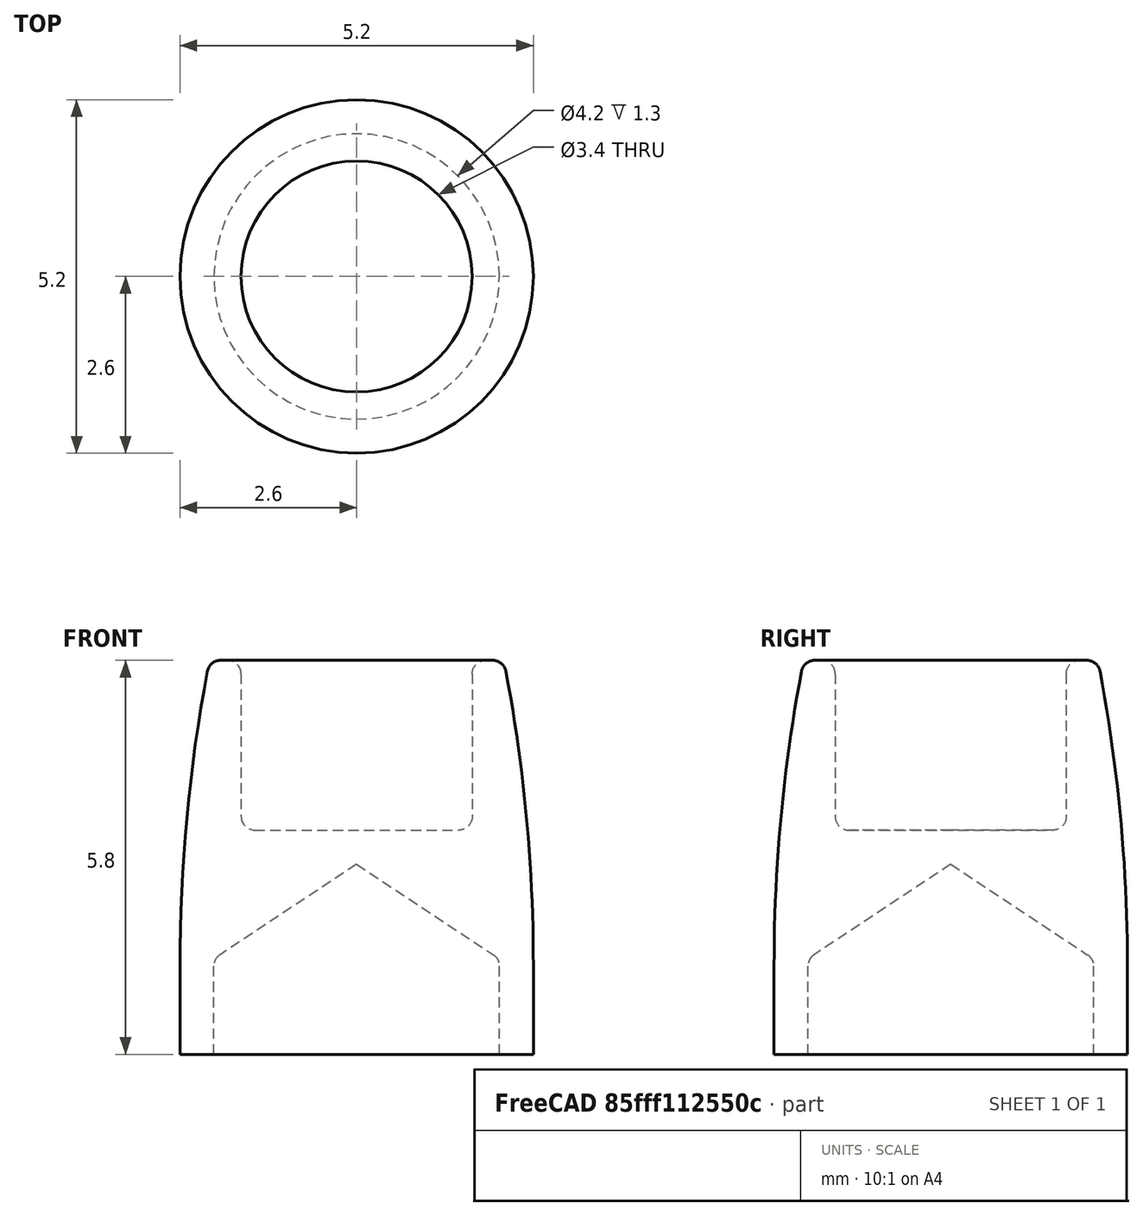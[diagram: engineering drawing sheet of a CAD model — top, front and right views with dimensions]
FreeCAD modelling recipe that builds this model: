
FCSTD DOCUMENT  (FreeCAD 0.18R16093 +53 (Git))
Label: MagnetHolderD3.6L5.5
License: All rights reserved
LicenseURL: http://en.wikipedia.org/wiki/All_rights_reserved
objects: Sketcher::SketchObject×1, PartDesign::Revolution×1, PartDesign::Body×1
note: 4 computed .brp shape members not serialized (recipe doc carries the construction recipe); baked Part::Feature solids carry a one-line shape summary decoded from their .brp

FEATURE [Sketcher::SketchObject] Sketch
  MapMode = 5
  Placement = pos=(0,0,0) rot=(1,0,0;1.5708rad)
  Support = -> [XZ_Plane]
  sketch-geometry (13):
    g0: LineSegment StartX=-2.6 StartY=0 StartZ=0 EndX=-2.6 EndY=-1.3 EndZ=0
    g1: LineSegment StartX=-2.6 StartY=-1.3 StartZ=0 EndX=-2.1 EndY=-1.3 EndZ=0
    g2: LineSegment StartX=-2.1 StartY=-1.3 StartZ=0 EndX=-2.1 EndY=0 EndZ=0
    g3: ArcOfCircle CenterX=44.5667 CenterY=0 CenterZ=0 NormalX=0 NormalY=0 NormalZ=1 AngleXU=0 Radius=47.1667 StartAngle=3.02851 EndAngle=3.14159
    g4: LineSegment StartX=-1.8 StartY=5.3 StartZ=0 EndX=-1.8 EndY=3.2 EndZ=0
    g5: LineSegment StartX=0 StartY=3 StartZ=0 EndX=0 EndY=2.5 EndZ=0
    g6: ArcOfCircle CenterX=-2.1 CenterY=5.3 CenterZ=0 NormalX=0 NormalY=0 NormalZ=1 AngleXU=0 Radius=0.2 StartAngle=1.5708 EndAngle=3.02851
    g7: LineSegment StartX=-2.1 StartY=5.5 StartZ=0 EndX=-2 EndY=5.5 EndZ=0
    g8: ArcOfCircle CenterX=-2 CenterY=5.3 CenterZ=0 NormalX=0 NormalY=0 NormalZ=1 AngleXU=0 Radius=0.2 StartAngle=2e-15 EndAngle=1.5708
    g9: ArcOfCircle CenterX=-1.6 CenterY=3.2 CenterZ=0 NormalX=0 NormalY=0 NormalZ=1 AngleXU=0 Radius=0.2 StartAngle=3.14159 EndAngle=4.71239
    g10: LineSegment StartX=-1.6 StartY=3 StartZ=0 EndX=0 EndY=3 EndZ=0
    g11: LineSegment StartX=0 StartY=2.5 StartZ=0 EndX=-2.0512 EndY=0.130913 EndZ=0
    g12: ArcOfCircle CenterX=-1.9 CenterY=0 CenterZ=0 NormalX=0 NormalY=0 NormalZ=1 AngleXU=0 Radius=0.2 StartAngle=2.42799 EndAngle=3.14159
  constraints (35):
    c: Vertical(g0)
    c: Vertical(g2)
    c: Coincident(g1,g0)
    c: Coincident(g2,g1)
    c: Horizontal(g1)
    c: PointOnObject(g2,g-1)
    c: Tangent(g3,g0) = -1.5708
    c: DistanceX(g1,g1) = 0.5
    c: DistanceX(g2) = -2.1
    c: DistanceY(g2,g2) = 1.3
    c: PointOnObject(g5,g-2)
    c: Vertical(g4)
    c: Vertical(g5)
    c: Radius(g6) = 0.2
    c: Horizontal(g7)
    c: Tangent(g6,g7) = 1.5708
    c: Tangent(g8,g7) = 1.5708
    c: DistanceY(g7) = 5.5
    c: Tangent(g4,g8) = 1.5708
    c: DistanceX(g4) = -1.8
    c: Equal(g6,g8)
    c: Horizontal(g10)
    c: Tangent(g9,g4) = -1.5708
    c: Tangent(g9,g10) = -1.5708
    c: Coincident(g10,g5)
    c: Equal(g8,g9)
    c: DistanceY(g5,g5) = 0.5
    c: DistanceY(g9,g7) = 2.5
    c: Tangent(g3,g6) = -1.5708
    c: DistanceX(g7,g7) = 0.1
    c: PointOnObject(g0,g-1)
    c: Coincident(g11,g5)
    c: Tangent(g12,g11) = -1.5708
    c: Tangent(g12,g2) = 1.5708
    c: Equal(g12,g9)
FEATURE [PartDesign::Revolution] Revolution
  Angle = 360
  Axis = (0,2e-16,1)
  Base = (0,0,0)
  Placement = pos=(0,0,0) rot=(1,0,0;1.5708rad)
  Profile = -> Sketch
  ReferenceAxis = -> Sketch [V_Axis]
FEATURE [PartDesign::Body] Body
  Group = -> [Sketch,Revolution]
  Origin = -> Origin
  Tip = -> Revolution
